# Revit family: АЙСБЕРГ
name_source: partatom
category: Осветительные приборы
units: mm (PartAtom-declared; Revit-internal decimal feet)

## family parameters
Всегда вертикально = Нет
Источник света = Да
На основе рабочей плоскости = Да
Общий = Нет
При загрузке вырезать с полостями = Нет
Размер круглого соединителя = Использовать диаметр
Тип детали = Нормальный
Точка расчета площади = Да

## types (8) — shared parameters
ADSK_Единица измерения = шт.
ADSK_Завод-изготовитель = ЗАО «Центрстройсвет»
ADSK_Классификация нагрузок = Прочее
ADSK_Количество фаз = 1
ADSK_Количество фаз числовое = 1
ADSK_Коэффициент мощности = 0.92
ADSK_Масса = 2.2
ADSK_Напряжение = 230 В
ADSK_Ток = 0 А
URL = http://csvt.ru
l = 20 мм
Видимая форма излучения при визуализации = Да
Высота = 100 мм
Длина = 1270 мм
Изготовитель = ЗАО «Центрстройсвет»
Излучение по длине прямоугольника = 1250 мм
Излучение по ширине прямоугольника = 132 мм
Материал коробки = <По категории>
Материал светильника = RAL 9006
Материал стекла = RAL 9001
Отметка по умолчанию = 1219 мм
Светофильтр = 16777215
Смещение цветовой температуры при затухании лампы = <Нет>
Угол наклона = 90.00°
Ширина = 152 мм

## per-type parameters (varying)
| type | ADSK_Код изделия | ADSK_Наименование | ADSK_Номинальная мощность | ADSK_Обозначение | ADSK_Полная мощность | Файл фотометрической сетки |
| CSVT Айсберг-38  (IP65, 5000К ) | ЦБ000001207 | Светодиодный пылевлагозащищенный светильник CSVT Айсберг-38 (IP65, 5000К) | 38 Вт | CSVT Айсберг-38 (IP65, 5000К) | 41 В·А | CSVT Iceberg-38.ies |
| CSVT Айсберг-38  (IP65, 5000К ) c БАП на 1 час. | ЦБ000003061 | Светодиодный пылевлагозащищенный светильник CSVT Айсберг-38  (IP65, 5000К ) c БАП на 1 час | 38 Вт | CSVT Айсберг-38 (IP65, 5000К ) | 41 В·А | CSVT Iceberg-38.ies |
| CSVT Айсберг-38  (IP65, 5000К ) c БАП на 3 час. | ЦБ000003051 | Светодиодный пылевлагозащищенный светильник CSVT Айсберг-38  (IP65, 5000К ) c БАП на 3 часа | 38 Вт | CSVT Айсберг-38 (IP65, 5000К ) | 41 В·А | CSVT Iceberg-38.ies |
| CSVT Айсберг-57  (IP65, 5000К ) | ЦБ000008788 | Светодиодный пылевлагозащищенный светильник CSVT Айсберг-57  (IP65, 5000К ) | 57 Вт | CSVT Айсберг-57 (IP65, 5000К ) | 62 В·А | CSVT Iceberg-57.ies |
| CSVT Айсберг-38/MILKY  (IP65, 5000К ) c БАП на 1 час. | ЦБ000009150 | Светодиодный пылевлагозащищенный светильник CSVT Айсберг-38/MILKY  (IP65, 5000К ) c БАП на 1 час | 38 Вт | CSVT Айсберг-38/MILKY (IP65, 5000К ) | 41 В·А | CSVT Iceberg-38Milky.ies |
| CSVT Айсберг-38/MILKY  (IP65, 5000К ) c БАП на 3 час. | ЦБ000009151 | Светодиодный пылевлагозащищенный светильник CSVT Айсберг-38/MILKY  (IP65, 5000К ) c БАП на 3 часа | 38 Вт | CSVT Айсберг-38/MILKY (IP65, 5000К ) | 41 В·А | CSVT Iceberg-38Milky.ies |
| CSVT Айсберг-57/MILKY  (IP65, 5000К ) | ЦБ000009193 | Светодиодный пылевлагозащищенный светильник CSVT Айсберг-57/MILKY  (IP65, 5000К ) | 57 Вт | CSVT Айсберг-57/MILKY (IP65, 5000К ) | 62 В·А | CSVT Iceberg-57Milky.ies |
| CSVT Айсберг-38/MILKY (IP65, 5000К ) | ЦБ000009149 | Светодиодный пылевлагозащищенный светильник CSVT Айсберг-38 (IP65, 5000К) | 38 Вт | CSVT Айсберг-38 (IP65, 5000К) | 41 В·А | CSVT Iceberg-38Milky.ies |
